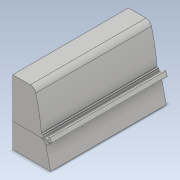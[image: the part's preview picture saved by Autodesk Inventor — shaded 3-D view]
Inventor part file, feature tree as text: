
AUTODESK INVENTOR PART (.ipt)
format: ipt  version: 2022 (Build 260153000, 153)  size: 183,296 bytes
history: native  units: mm
features: extrude x2, fillet x2, sketch x1, other x1
ambient origin geometry x8: Origin, YZ Plane, XZ Plane, XY Plane, X Axis, Y Axis, Z Axis, Center Point
bodies: Body1 (feature_tree), Body2 (feature_tree)
feature tree (6):
  extrude  "擠出1"  Depth=13.0mm
  fillet  "圓角2"  Radius=1.7mm
  extrude  "擠出2"  Depth=1.7mm
  fillet  "圓角3"  Radius=1.0mm
  sketch  "草圖4"
  other  "實體3"
